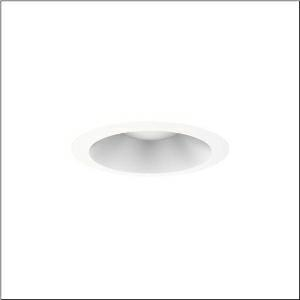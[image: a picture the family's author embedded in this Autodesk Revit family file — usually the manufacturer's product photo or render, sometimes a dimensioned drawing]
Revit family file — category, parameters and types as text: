
# Revit family: lunis_31_midi_51dn16dg42
name_source: partatom
category: Lighting Fixtures
units: mm (PartAtom-declared; Revit-internal decimal feet)

## family parameters
Cut with Voids When Loaded = No
Host = Face
Light Source = No
Part Type = Normal
Room Calculation Point = No
Round Connector Dimension = Use Diameter
Shared = No

## types (1)
- Lunis 31 midi (1 x LED, 2150 lm, 17 W, 4000K)
    Apparent Load = 17 VA
    CIE Flux Codes = 64 93 99 100 100
    Color Rendering = 80
    Color Temperature = 4000K
    Default Elevation = 1800 mm
    Description = Lunis 31,  midi, downlight, light control with reflector, light emission: direct distribution, LED rated luminous flux: 2.150lm, light colour: 840, control gear: ECG DALI, mains connection: 220..240V, AC, 50/60Hz, housing, white, protection rating (complete): IP20, insulation class (complete): insulation class II (safety insulation), certification: CE, packaging unit: 1 piece
    Height = 0 mm  [stored 0 ft]
    Lamp = 1 x LED
    Lamp Light Flux = 2150 lm
    Lamp Power = 17 W
    Lamp count = 1
    Length = 259 mm
    Luminous efficacy = 126 lm/W
    Manufacturer = Siteco
    ModVariant = No
    Model = 51DN16DG42
    Mounting Place = Ceiling
    Mounting Type = Recessed
    Number of Poles = 1
    OnlyDefault = Yes
    Power Factor = 1
    Product Name = Lunis 31 midi
    Product group = downlight | ceiling recessed
    ProductGroupID = 402
    Protection Class = Protection class II
    Protection Degree = IP 20
    RLX_Detail_Level = 1
    RlxData = <blob elided: 23769 chars, md5=65bc7460>
    Socket = socket
    Standby Power = 0 W
    System Light Flux = 2150 lm
    System Power = 17 W
    Type Comments = Product without accessories
    Type Image = l_1006711.jpg
    URL = http://relux.com
    VarID = ---
    Voltage = 0 V
    Weight = 0.00 kg
    Width = 0 mm  [stored 0 ft]

note: [stored X ft] marks values corroborated as IEEE doubles in the binary element streams (Revit-internal decimal feet)

## geometry (parser evidence)
native form markers: Blend x4, Sweep x12
no freeform markers — native parametric forms only
